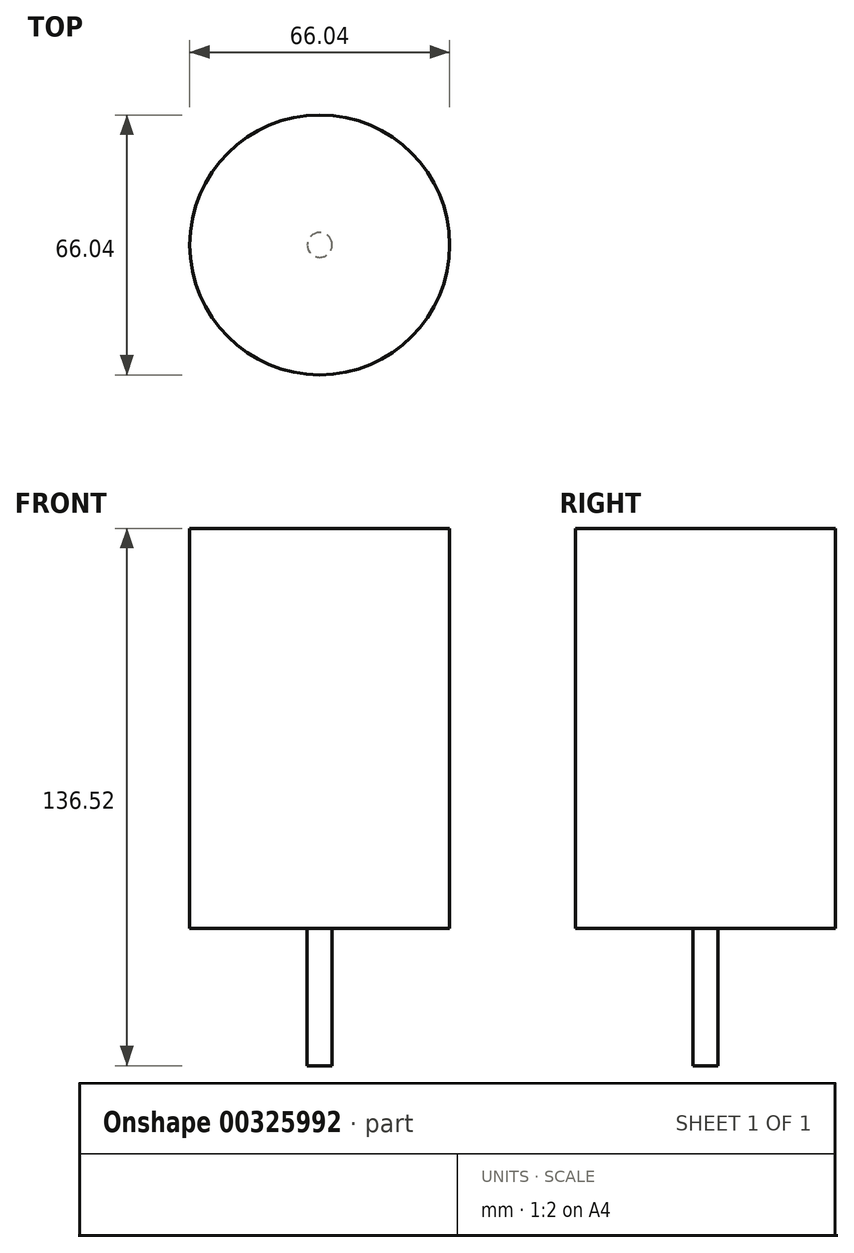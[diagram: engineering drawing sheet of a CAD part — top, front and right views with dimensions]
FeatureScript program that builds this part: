
annotation { "Feature Type Name" : "Feature", "Feature Type Description" : "" }
export const myFeature = defineFeature(function(context is Context, id is Id, definition is map)
    precondition{}
    {
        {
            var Q0;
            Q0=qCreatedBy(makeId("Front.planeOp"),FACE);
            var sketch = newSketch(context, id + "F0", { "sketchPlane" : qUnion([Q0])});
            skLineSegment(sketch, "E0", {"start": v(-33.02, 63.02) * mm, "end": v(-33.02, -38.58) * mm});
            skLineSegment(sketch, "E1", {"start": v(-3.17, -38.58) * mm, "end": v(-33.02, -38.58) * mm});
            skLineSegment(sketch, "E2", {"start": v(-3.17, -38.58) * mm, "end": v(-3.17, -73.5) * mm});
            skLineSegment(sketch, "E3", {"start": v(0, -73.5) * mm, "end": v(0, 63.02) * mm});
            skLineSegment(sketch, "E4", {"start": v(0, 63.02) * mm, "end": v(-33.02, 63.02) * mm});
            skLineSegment(sketch, "E5", {"start": v(0, -73.5) * mm, "end": v(-3.17, -73.5) * mm});
            skSolve(sketch);
        }
        {
            var Q0;
            Q0=makeQuery(id+"F0.imprint","IMPRINT",FACE,{"disambiguationData":[TD([[makeQuery(id+"F0.imprint","IMPRINT",EDGE,{"derivedFrom":sQuery(id+"F0.wireOp",EDGE,"E0")}),1.0]])]});
            var Q1;
            Q1=sQuery(id+"F0.wireOp",EDGE,"E4");
            var Q2;
            Q2=sQuery(id+"F0.wireOp",EDGE,"E0");
            var Q3;
            Q3=sQuery(id+"F0.wireOp",EDGE,"E1");
            var Q4;
            Q4=sQuery(id+"F0.wireOp",EDGE,"E2");
            var Q5;
            Q5=sQuery(id+"F0.wireOp",EDGE,"E5");
            var Q6;
            Q6=sQuery(id+"F0.wireOp",EDGE,"E3");
            revolve(context, id + "F1", {"entities" : qUnion([Q0]), "surfaceEntities" : qUnion([Q1, Q2, Q3, Q4, Q5]), "axis" : qUnion([Q6]), "revolveType" : RevolveType.FULL});
        }
    });
